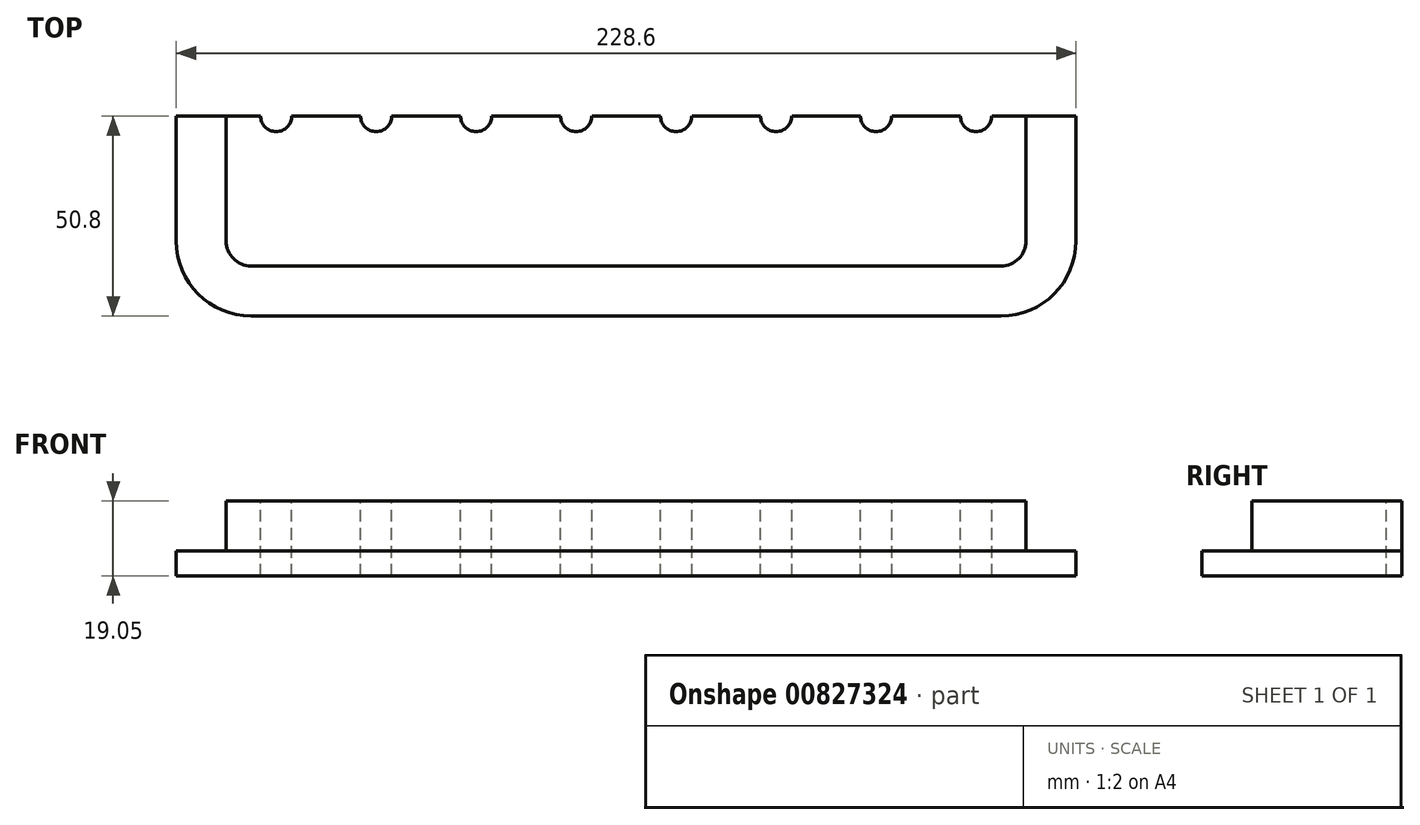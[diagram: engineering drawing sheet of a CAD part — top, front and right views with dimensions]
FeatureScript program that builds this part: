
annotation { "Feature Type Name" : "Feature", "Feature Type Description" : "" }
export const myFeature = defineFeature(function(context is Context, id is Id, definition is map)
    precondition{}
    {
        {
            var Q0;
            Q0=qCreatedBy(makeId("Top.planeOp"),FACE);
            var sketch = newSketch(context, id + "F0", { "sketchPlane" : qUnion([Q0])});
            skLineSegment(sketch, "E0.bottom", {"start": v(19.05, 0) * mm, "end": v(209.55, 0) * mm});
            skLineSegment(sketch, "E0.left", {"start": v(0, 19.05) * mm, "end": v(0, 50.8) * mm});
            skLineSegment(sketch, "E0.right", {"start": v(228.6, 19.05) * mm, "end": v(228.6, 50.8) * mm});
            skPoint(sketch, "E1.visualSharp", {"position": v(228.6, 0) * mm});
            skArc(sketch, "E1.filletArc", {"start": v(209.55, 0) * mm, "mid": v(223.02, 5.58) * mm, "end": v(228.6, 19.05) * mm});
            skPoint(sketch, "E2.visualSharp", {"position": v(0, 0) * mm});
            skArc(sketch, "E2.filletArc", {"start": v(0, 19.05) * mm, "mid": v(5.58, 5.58) * mm, "end": v(19.05, 0) * mm});
            skLineSegment(sketch, "E3", {"start": v(0, 50.8) * mm, "end": v(228.6, 50.8) * mm});
            skSolve(sketch);
        }
        {
            var Q0;
            Q0=makeQuery(id+"F0.imprint","IMPRINT",FACE,{"disambiguationData":[TD([[makeQuery(id+"F0.imprint","IMPRINT",EDGE,{"derivedFrom":sQuery(id+"F0.wireOp",EDGE,"E0.bottom")}),1.0]])]});
            extrude(context, id + "F1", {"entities" : qUnion([Q0]), "depth" : 6.35 * mm, "offsetDistance" : 25.4 * mm});
        }
        {
            var Q0;
            Q0=makeQuery(id+"F1.opExtrude","CAP_FACE",FACE,{"disambiguationData":[OSD([sQuery(id+"F0.wireOp",EDGE,"E0.bottom"),sQuery(id+"F0.wireOp",EDGE,"E0.left"),sQuery(id+"F0.wireOp",EDGE,"E0.right"),sQuery(id+"F0.wireOp",EDGE,"E1.filletArc"),sQuery(id+"F0.wireOp",EDGE,"E2.filletArc"),sQuery(id+"F0.wireOp",EDGE,"E3")])],"isStart":false});
            var sketch = newSketch(context, id + "F2", { "sketchPlane" : qUnion([Q0])});
            skLineSegment(sketch, "E4.0", {"start": v(12.7, 19.05) * mm, "end": v(12.7, 50.8) * mm});
            skLineSegment(sketch, "E4.1", {"start": v(215.9, 19.05) * mm, "end": v(215.9, 50.8) * mm});
            skArc(sketch, "E4.2", {"start": v(209.55, 12.7) * mm, "mid": v(214.04, 14.56) * mm, "end": v(215.9, 19.05) * mm});
            skLineSegment(sketch, "E4.3", {"start": v(19.05, 12.7) * mm, "end": v(209.55, 12.7) * mm});
            skArc(sketch, "E4.4", {"start": v(12.7, 19.05) * mm, "mid": v(14.56, 14.56) * mm, "end": v(19.05, 12.7) * mm});
            skLineSegment(sketch, "E5", {"start": v(12.7, 50.8) * mm, "end": v(215.9, 50.8) * mm});
            skSolve(sketch);
        }
        {
            var Q0;
            Q0=makeQuery(id+"F2.imprint","IMPRINT",FACE,{"disambiguationData":[TD([[makeQuery(id+"F2.imprint","IMPRINT",EDGE,{"derivedFrom":sQuery(id+"F2.wireOp",EDGE,"E4.0")}),-1.0]])]});
            extrude(context, id + "F3", {"entities" : qUnion([Q0]), "operationType" : NewBodyOperationType.ADD, "depth" : 12.7 * mm, "offsetDistance" : 25.4 * mm});
        }
        {
            var Q0;
            Q0=makeQuery(id+"F3.opExtrude","CAP_FACE",FACE,{"disambiguationData":[OSD([sQuery(id+"F2.wireOp",EDGE,"E4.0"),sQuery(id+"F2.wireOp",EDGE,"E4.1"),sQuery(id+"F2.wireOp",EDGE,"E4.2"),sQuery(id+"F2.wireOp",EDGE,"E4.3"),sQuery(id+"F2.wireOp",EDGE,"E4.4"),sQuery(id+"F2.wireOp",EDGE,"E5")])],"isStart":false});
            var sketch = newSketch(context, id + "F4", { "sketchPlane" : qUnion([Q0])});
            skCircle(sketch, "E6", {"center": v(203.2, 50.8) * mm, "radius": 3.97 * mm});
            skCircle(sketch, "E7.1.0.0", {"center": v(177.8, 50.8) * mm, "radius": 3.97 * mm});
            skCircle(sketch, "E7.2.0.0", {"center": v(152.4, 50.8) * mm, "radius": 3.97 * mm});
            skCircle(sketch, "E7.3.0.0", {"center": v(127, 50.8) * mm, "radius": 3.97 * mm});
            skCircle(sketch, "E7.4.0.0", {"center": v(101.6, 50.8) * mm, "radius": 3.97 * mm});
            skCircle(sketch, "E7.5.0.0", {"center": v(76.2, 50.8) * mm, "radius": 3.97 * mm});
            skCircle(sketch, "E7.6.0.0", {"center": v(50.8, 50.8) * mm, "radius": 3.97 * mm});
            skCircle(sketch, "E7.7.0.0", {"center": v(25.4, 50.8) * mm, "radius": 3.97 * mm});
            skLineSegment(sketch, "E7.direction1", {"start": v(203.2, 50.8) * mm, "end": v(177.8, 50.8) * mm, "construction": true});
            skSolve(sketch);
        }
        {
            var Q0;
            {var subQ0=sQuery(id+"F4.wireOp",EDGE,"E7.7.0.0");var subQ1=makeQuery(id+"F3.opExtrude","CAP_EDGE",EDGE,{"disambiguationData":[OSD([sQuery(id+"F2.wireOp",EDGE,"E5")])],"isStart":false});var subQ2=makeQuery(id+"F4.imprint","INTERSECT",VERTEX,{"disambiguationData":[OD(0.0)],"derivedFrom":[subQ1,subQ0]});Q0=makeQuery(id+"F4.imprint","IMPRINT",FACE,{"disambiguationData":[TD([[makeQuery(id+"F4.imprint","IMPRINT",EDGE,{"disambiguationData":[TD([[subQ2,1.0]])],"derivedFrom":subQ0}),1.0]])]});}
            var Q1;
            {var subQ0=sQuery(id+"F4.wireOp",EDGE,"E7.7.0.0");var subQ1=makeQuery(id+"F3.opExtrude","CAP_EDGE",EDGE,{"disambiguationData":[OSD([sQuery(id+"F2.wireOp",EDGE,"E5")])],"isStart":false});var subQ2=makeQuery(id+"F4.imprint","INTERSECT",VERTEX,{"disambiguationData":[OD(0.0)],"derivedFrom":[subQ1,subQ0]});Q1=makeQuery(id+"F4.imprint","IMPRINT",FACE,{"disambiguationData":[TD([[makeQuery(id+"F4.imprint","IMPRINT",EDGE,{"disambiguationData":[TD([[subQ2,-1.0]])],"derivedFrom":subQ0}),1.0]])]});}
            var Q2;
            {var subQ0=sQuery(id+"F4.wireOp",EDGE,"E7.6.0.0");var subQ1=makeQuery(id+"F3.opExtrude","CAP_EDGE",EDGE,{"disambiguationData":[OSD([sQuery(id+"F2.wireOp",EDGE,"E5")])],"isStart":false});var subQ2=makeQuery(id+"F4.imprint","INTERSECT",VERTEX,{"disambiguationData":[OD(0.0)],"derivedFrom":[subQ1,subQ0]});Q2=makeQuery(id+"F4.imprint","IMPRINT",FACE,{"disambiguationData":[TD([[makeQuery(id+"F4.imprint","IMPRINT",EDGE,{"disambiguationData":[TD([[subQ2,1.0]])],"derivedFrom":subQ0}),1.0]])]});}
            var Q3;
            {var subQ0=sQuery(id+"F4.wireOp",EDGE,"E7.6.0.0");var subQ1=makeQuery(id+"F3.opExtrude","CAP_EDGE",EDGE,{"disambiguationData":[OSD([sQuery(id+"F2.wireOp",EDGE,"E5")])],"isStart":false});var subQ2=makeQuery(id+"F4.imprint","INTERSECT",VERTEX,{"disambiguationData":[OD(0.0)],"derivedFrom":[subQ1,subQ0]});Q3=makeQuery(id+"F4.imprint","IMPRINT",FACE,{"disambiguationData":[TD([[makeQuery(id+"F4.imprint","IMPRINT",EDGE,{"disambiguationData":[TD([[subQ2,-1.0]])],"derivedFrom":subQ0}),1.0]])]});}
            var Q4;
            {var subQ0=sQuery(id+"F4.wireOp",EDGE,"E7.5.0.0");var subQ1=makeQuery(id+"F3.opExtrude","CAP_EDGE",EDGE,{"disambiguationData":[OSD([sQuery(id+"F2.wireOp",EDGE,"E5")])],"isStart":false});var subQ2=makeQuery(id+"F4.imprint","INTERSECT",VERTEX,{"disambiguationData":[OD(0.0)],"derivedFrom":[subQ1,subQ0]});Q4=makeQuery(id+"F4.imprint","IMPRINT",FACE,{"disambiguationData":[TD([[makeQuery(id+"F4.imprint","IMPRINT",EDGE,{"disambiguationData":[TD([[subQ2,-1.0]])],"derivedFrom":subQ0}),1.0]])]});}
            var Q5;
            {var subQ0=sQuery(id+"F4.wireOp",EDGE,"E6");var subQ1=makeQuery(id+"F3.opExtrude","CAP_EDGE",EDGE,{"disambiguationData":[OSD([sQuery(id+"F2.wireOp",EDGE,"E5")])],"isStart":false});var subQ2=makeQuery(id+"F4.imprint","INTERSECT",VERTEX,{"disambiguationData":[OD(0.0)],"derivedFrom":[subQ1,subQ0]});Q5=makeQuery(id+"F4.imprint","IMPRINT",FACE,{"disambiguationData":[TD([[makeQuery(id+"F4.imprint","IMPRINT",EDGE,{"disambiguationData":[TD([[subQ2,-1.0]])],"derivedFrom":subQ0}),1.0]])]});}
            var Q6;
            {var subQ0=sQuery(id+"F4.wireOp",EDGE,"E7.1.0.0");var subQ1=makeQuery(id+"F3.opExtrude","CAP_EDGE",EDGE,{"disambiguationData":[OSD([sQuery(id+"F2.wireOp",EDGE,"E5")])],"isStart":false});var subQ2=makeQuery(id+"F4.imprint","INTERSECT",VERTEX,{"disambiguationData":[OD(0.0)],"derivedFrom":[subQ1,subQ0]});Q6=makeQuery(id+"F4.imprint","IMPRINT",FACE,{"disambiguationData":[TD([[makeQuery(id+"F4.imprint","IMPRINT",EDGE,{"disambiguationData":[TD([[subQ2,-1.0]])],"derivedFrom":subQ0}),1.0]])]});}
            var Q7;
            {var subQ0=sQuery(id+"F4.wireOp",EDGE,"E7.2.0.0");var subQ1=makeQuery(id+"F3.opExtrude","CAP_EDGE",EDGE,{"disambiguationData":[OSD([sQuery(id+"F2.wireOp",EDGE,"E5")])],"isStart":false});var subQ2=makeQuery(id+"F4.imprint","INTERSECT",VERTEX,{"disambiguationData":[OD(0.0)],"derivedFrom":[subQ1,subQ0]});Q7=makeQuery(id+"F4.imprint","IMPRINT",FACE,{"disambiguationData":[TD([[makeQuery(id+"F4.imprint","IMPRINT",EDGE,{"disambiguationData":[TD([[subQ2,-1.0]])],"derivedFrom":subQ0}),1.0]])]});}
            var Q8;
            {var subQ0=sQuery(id+"F4.wireOp",EDGE,"E7.3.0.0");var subQ1=makeQuery(id+"F3.opExtrude","CAP_EDGE",EDGE,{"disambiguationData":[OSD([sQuery(id+"F2.wireOp",EDGE,"E5")])],"isStart":false});var subQ2=makeQuery(id+"F4.imprint","INTERSECT",VERTEX,{"disambiguationData":[OD(0.0)],"derivedFrom":[subQ1,subQ0]});Q8=makeQuery(id+"F4.imprint","IMPRINT",FACE,{"disambiguationData":[TD([[makeQuery(id+"F4.imprint","IMPRINT",EDGE,{"disambiguationData":[TD([[subQ2,-1.0]])],"derivedFrom":subQ0}),1.0]])]});}
            var Q9;
            {var subQ0=sQuery(id+"F4.wireOp",EDGE,"E7.4.0.0");var subQ1=makeQuery(id+"F3.opExtrude","CAP_EDGE",EDGE,{"disambiguationData":[OSD([sQuery(id+"F2.wireOp",EDGE,"E5")])],"isStart":false});var subQ2=makeQuery(id+"F4.imprint","INTERSECT",VERTEX,{"disambiguationData":[OD(0.0)],"derivedFrom":[subQ1,subQ0]});Q9=makeQuery(id+"F4.imprint","IMPRINT",FACE,{"disambiguationData":[TD([[makeQuery(id+"F4.imprint","IMPRINT",EDGE,{"disambiguationData":[TD([[subQ2,1.0]])],"derivedFrom":subQ0}),1.0]])]});}
            var Q10;
            {var subQ0=sQuery(id+"F4.wireOp",EDGE,"E7.5.0.0");var subQ1=makeQuery(id+"F3.opExtrude","CAP_EDGE",EDGE,{"disambiguationData":[OSD([sQuery(id+"F2.wireOp",EDGE,"E5")])],"isStart":false});var subQ2=makeQuery(id+"F4.imprint","INTERSECT",VERTEX,{"disambiguationData":[OD(0.0)],"derivedFrom":[subQ1,subQ0]});Q10=makeQuery(id+"F4.imprint","IMPRINT",FACE,{"disambiguationData":[TD([[makeQuery(id+"F4.imprint","IMPRINT",EDGE,{"disambiguationData":[TD([[subQ2,1.0]])],"derivedFrom":subQ0}),1.0]])]});}
            var Q11;
            {var subQ0=sQuery(id+"F4.wireOp",EDGE,"E6");var subQ1=makeQuery(id+"F3.opExtrude","CAP_EDGE",EDGE,{"disambiguationData":[OSD([sQuery(id+"F2.wireOp",EDGE,"E5")])],"isStart":false});var subQ2=makeQuery(id+"F4.imprint","INTERSECT",VERTEX,{"disambiguationData":[OD(0.0)],"derivedFrom":[subQ1,subQ0]});Q11=makeQuery(id+"F4.imprint","IMPRINT",FACE,{"disambiguationData":[TD([[makeQuery(id+"F4.imprint","IMPRINT",EDGE,{"disambiguationData":[TD([[subQ2,1.0]])],"derivedFrom":subQ0}),1.0]])]});}
            var Q12;
            {var subQ0=sQuery(id+"F4.wireOp",EDGE,"E7.1.0.0");var subQ1=makeQuery(id+"F3.opExtrude","CAP_EDGE",EDGE,{"disambiguationData":[OSD([sQuery(id+"F2.wireOp",EDGE,"E5")])],"isStart":false});var subQ2=makeQuery(id+"F4.imprint","INTERSECT",VERTEX,{"disambiguationData":[OD(0.0)],"derivedFrom":[subQ1,subQ0]});Q12=makeQuery(id+"F4.imprint","IMPRINT",FACE,{"disambiguationData":[TD([[makeQuery(id+"F4.imprint","IMPRINT",EDGE,{"disambiguationData":[TD([[subQ2,1.0]])],"derivedFrom":subQ0}),1.0]])]});}
            var Q13;
            {var subQ0=sQuery(id+"F4.wireOp",EDGE,"E7.2.0.0");var subQ1=makeQuery(id+"F3.opExtrude","CAP_EDGE",EDGE,{"disambiguationData":[OSD([sQuery(id+"F2.wireOp",EDGE,"E5")])],"isStart":false});var subQ2=makeQuery(id+"F4.imprint","INTERSECT",VERTEX,{"disambiguationData":[OD(0.0)],"derivedFrom":[subQ1,subQ0]});Q13=makeQuery(id+"F4.imprint","IMPRINT",FACE,{"disambiguationData":[TD([[makeQuery(id+"F4.imprint","IMPRINT",EDGE,{"disambiguationData":[TD([[subQ2,1.0]])],"derivedFrom":subQ0}),1.0]])]});}
            var Q14;
            {var subQ0=sQuery(id+"F4.wireOp",EDGE,"E7.3.0.0");var subQ1=makeQuery(id+"F3.opExtrude","CAP_EDGE",EDGE,{"disambiguationData":[OSD([sQuery(id+"F2.wireOp",EDGE,"E5")])],"isStart":false});var subQ2=makeQuery(id+"F4.imprint","INTERSECT",VERTEX,{"disambiguationData":[OD(0.0)],"derivedFrom":[subQ1,subQ0]});Q14=makeQuery(id+"F4.imprint","IMPRINT",FACE,{"disambiguationData":[TD([[makeQuery(id+"F4.imprint","IMPRINT",EDGE,{"disambiguationData":[TD([[subQ2,1.0]])],"derivedFrom":subQ0}),1.0]])]});}
            var Q15;
            {var subQ0=sQuery(id+"F4.wireOp",EDGE,"E7.4.0.0");var subQ1=makeQuery(id+"F3.opExtrude","CAP_EDGE",EDGE,{"disambiguationData":[OSD([sQuery(id+"F2.wireOp",EDGE,"E5")])],"isStart":false});var subQ2=makeQuery(id+"F4.imprint","INTERSECT",VERTEX,{"disambiguationData":[OD(0.0)],"derivedFrom":[subQ1,subQ0]});Q15=makeQuery(id+"F4.imprint","IMPRINT",FACE,{"disambiguationData":[TD([[makeQuery(id+"F4.imprint","IMPRINT",EDGE,{"disambiguationData":[TD([[subQ2,-1.0]])],"derivedFrom":subQ0}),1.0]])]});}
            extrude(context, id + "F5", {"entities" : qUnion([Q0, Q1, Q2, Q3, Q4, Q5, Q6, Q7, Q8, Q9, Q10, Q11, Q12, Q13, Q14, Q15]), "operationType" : NewBodyOperationType.REMOVE, "oppositeDirection" : true, "depth" : 25.4 * mm, "offsetDistance" : 25.4 * mm});
        }
    });
